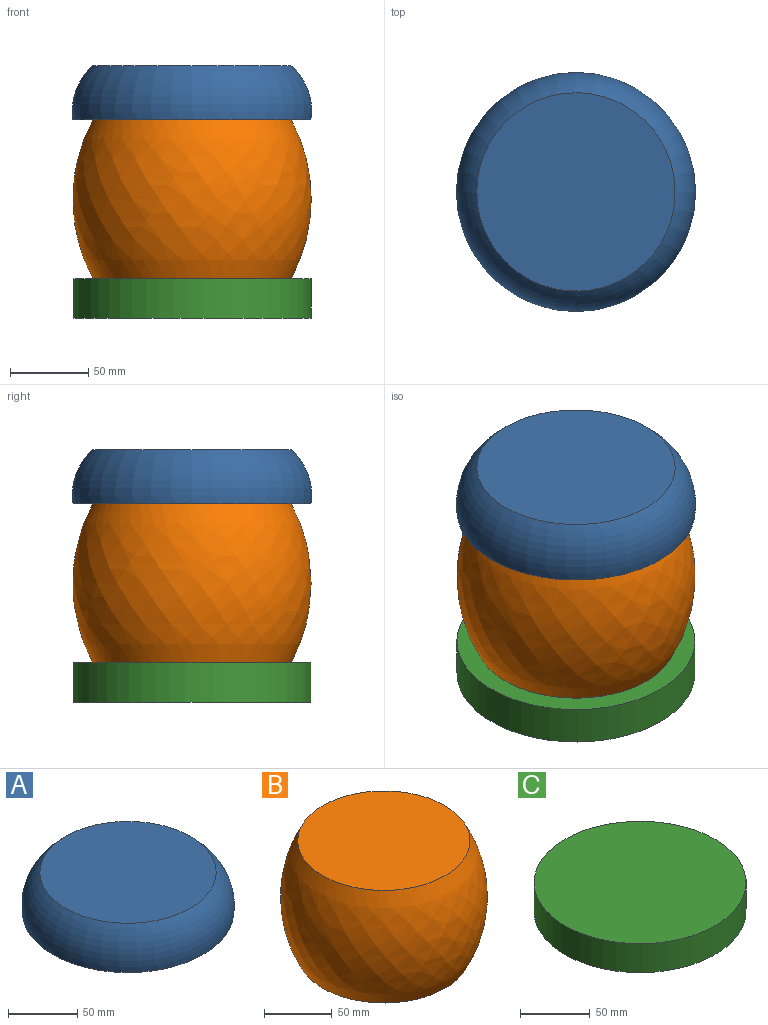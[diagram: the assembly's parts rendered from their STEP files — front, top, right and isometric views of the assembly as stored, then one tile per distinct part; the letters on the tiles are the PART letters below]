
ASSEMBLY  parts=3 mates=2
PART A: 3 faces, bbox 152.8x152.4x34.6 mm
  f0: plane 127x127mm, normal (0,0,1), area 12667.7mm2, adj f1
  f1: torus R=38.07mm, axis (0,0,-1), area 17554.1mm2, adj f0,f2
  f2: plane 152.4x152.4mm, normal (0,0,-1), area 18241.5mm2, adj f1
PART B: 3 faces, bbox 152.6x152.6x101.6 mm
  f0: plane 127x127mm, normal (0,0,1), area 12667.7mm2, adj f2
  f1: plane 127x127mm, normal (0,0,-1), area 12667.7mm2, adj f2
  f2: revolved ~152.64x152.64mm, area 47895.9mm2, adj f0,f1
PART C: 3 faces, bbox 152.4x152.4x25.4 mm
  f0: cylinder r=76.2mm len=152.4mm, axis (0,0,-1), area 12161mm2, adj f1,f2
  f1: plane 152.4x152.4mm, normal (0,0,1), area 18241.5mm2, adj f0
  f2: plane 152.4x152.4mm, normal (0,0,-1), area 18241.5mm2, adj f0
PLACE A t=(61.52,89.62,89.51)mm
PLACE B t=(61.52,89.62,33.69)mm
PLACE C t=(61.52,89.62,-37.49)mm fixed
MATE fastened B.f0 <-> A.f1  axis (0,0,1) through (61.52,89.62,89.51)mm
MATE fastened B.f1 <-> C.f0  axis (0,0,-1) through (61.52,89.62,-12.09)mm
